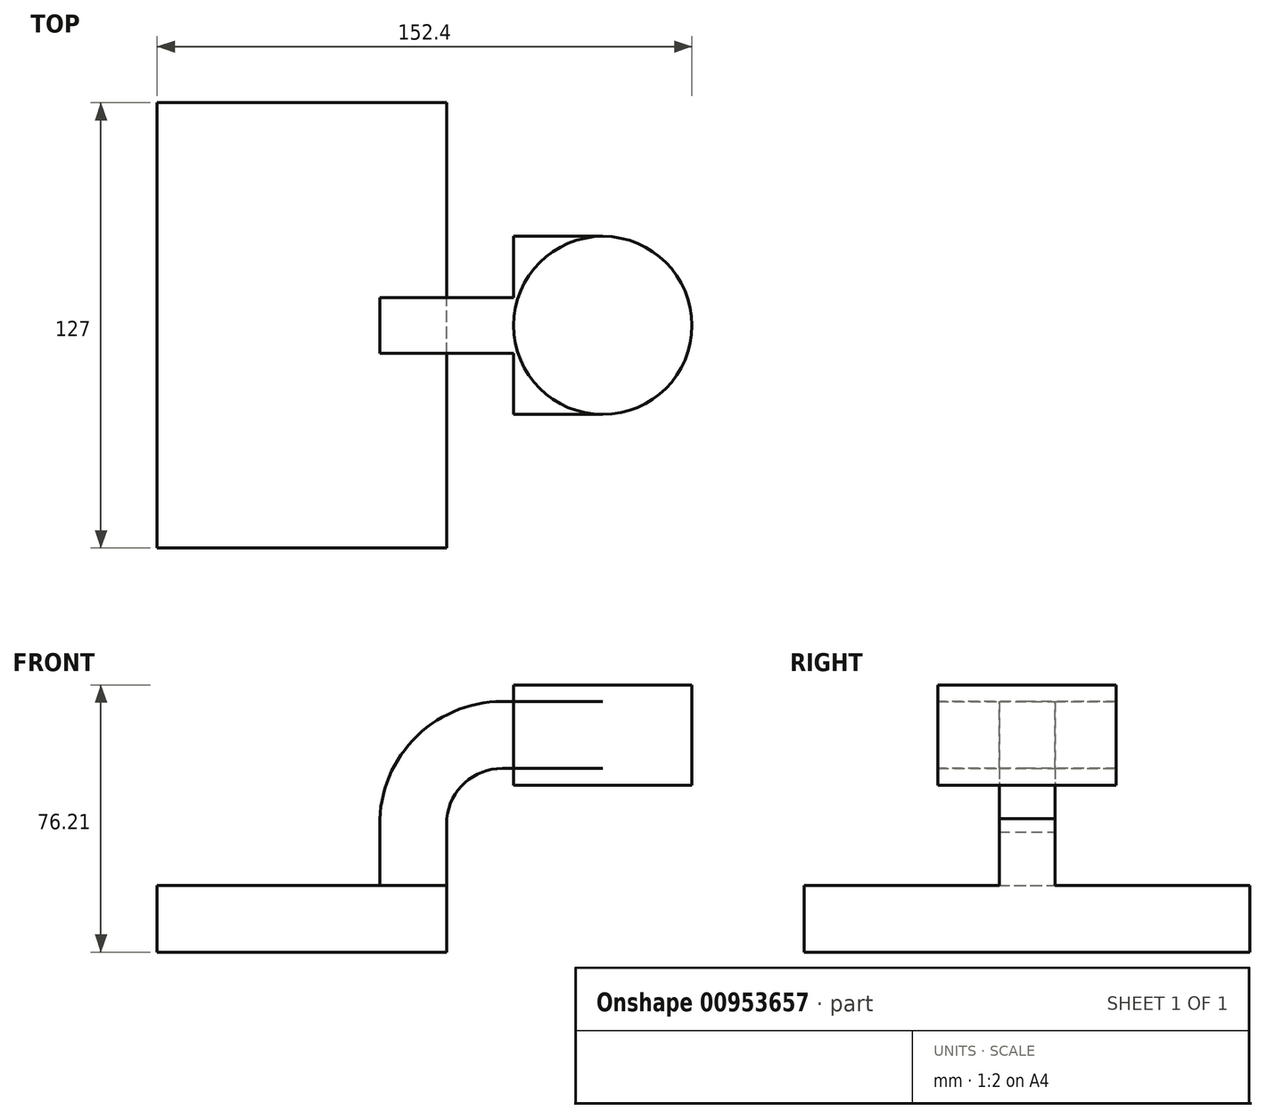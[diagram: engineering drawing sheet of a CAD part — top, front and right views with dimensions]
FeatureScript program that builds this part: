
annotation { "Feature Type Name" : "Feature", "Feature Type Description" : "" }
export const myFeature = defineFeature(function(context is Context, id is Id, definition is map)
    precondition{}
    {
        {
            var Q0;
            Q0=qCreatedBy(makeId("Front.planeOp"),FACE);
            var sketch = newSketch(context, id + "F0", { "sketchPlane" : qUnion([Q0])});
            skLineSegment(sketch, "E0.bottom", {"start": v(-41.28, -9.53) * mm, "end": v(41.28, -9.53) * mm});
            skLineSegment(sketch, "E0.top", {"start": v(-41.28, 9.53) * mm, "end": v(41.28, 9.53) * mm});
            skLineSegment(sketch, "E0.left", {"start": v(-41.28, -9.53) * mm, "end": v(-41.28, 9.53) * mm});
            skLineSegment(sketch, "E0.right", {"start": v(41.28, -9.53) * mm, "end": v(41.28, 9.53) * mm});
            skPoint(sketch, "E0.middle", {"position": v(0, 0) * mm});
            skLineSegment(sketch, "E1.bottom", {"start": v(60.33, 38.1) * mm, "end": v(111.12, 38.1) * mm});
            skLineSegment(sketch, "E1.top", {"start": v(60.33, 66.67) * mm, "end": v(111.12, 66.67) * mm});
            skLineSegment(sketch, "E1.left", {"start": v(60.33, 38.1) * mm, "end": v(60.33, 66.67) * mm});
            skLineSegment(sketch, "E1.right", {"start": v(111.12, 38.1) * mm, "end": v(111.12, 66.67) * mm});
            skPoint(sketch, "E1.middle", {"position": v(85.72, 52.39) * mm});
            skPoint(sketch, "E2.middle", {"position": v(41.28, 9.53) * mm});
            skArc(sketch, "E3", {"start": v(41.27, 28.54) * mm, "mid": v(46.4, 38.76) * mm, "end": v(57.08, 42.88) * mm});
            skLineSegment(sketch, "E4", {"start": v(57.08, 42.88) * mm, "end": v(85.72, 42.88) * mm});
            skLineSegment(sketch, "E5", {"start": v(41.28, 9.53) * mm, "end": v(41.27, 28.54) * mm});
            skArc(sketch, "E6.0", {"start": v(22.22, 24.72) * mm, "mid": v(31.59, 50.88) * mm, "end": v(57.08, 61.93) * mm});
            skLineSegment(sketch, "E6.1", {"start": v(22.23, 9.52) * mm, "end": v(22.22, 24.72) * mm});
            skLineSegment(sketch, "E7.0", {"start": v(57.08, 61.93) * mm, "end": v(85.72, 61.93) * mm});
            skLineSegment(sketch, "E8", {"start": v(85.72, 38.1) * mm, "end": v(85.72, 66.67) * mm});
            skFitSpline(sketch, "E9", {"points": [v(57.08, 61.93) * mm, v(-41.28, 9.53) * mm], "startDerivative": vector(-128.94, 14.74) * mm, "endDerivative": vector(-5.3, -85.67) * mm});
            skSolve(sketch);
        }
        {
            var Q0;
            Q0=makeQuery(id+"F0.imprint","IMPRINT",FACE,{"disambiguationData":[TD([[makeQuery(id+"F0.imprint","IMPRINT",EDGE,{"derivedFrom":sQuery(id+"F0.wireOp",EDGE,"E0.bottom")}),1.0]])]});
            extrude(context, id + "F1", {"entities" : qUnion([Q0]), "endBound" : BoundingType.SYMMETRIC, "depth" : 127 * mm, "offsetDistance" : 25.4 * mm});
        }
        {
            var Q0;
            {var subQ1=sQuery(id+"F0.wireOp",EDGE,"E3");Q0=makeQuery(id+"F0.imprint","IMPRINT",FACE,{"disambiguationData":[TD([[makeQuery(id+"F0.imprint","IMPRINT",EDGE,{"derivedFrom":subQ1}),1.0]])]});}
            var Q1;
            {var subQ0=sQuery(id+"F0.wireOp",EDGE,"E4");var subQ1=sQuery(id+"F0.wireOp",EDGE,"E1.left");var subQ2=makeQuery(id+"F0.imprint","INTERSECT",VERTEX,{"derivedFrom":[subQ1,subQ0]});Q1=makeQuery(id+"F0.imprint","IMPRINT",FACE,{"disambiguationData":[TD([[makeQuery(id+"F0.imprint","IMPRINT",EDGE,{"disambiguationData":[TD([[subQ2,-1.0]])],"derivedFrom":subQ1}),-1.0]])]});}
            extrude(context, id + "F2", {"entities" : qUnion([Q0, Q1]), "operationType" : NewBodyOperationType.ADD, "endBound" : BoundingType.SYMMETRIC, "depth" : 50.8 * mm, "offsetDistance" : 25.4 * mm});
        }
        {
            var Q0;
            Q0=makeQuery(id+"F0.imprint","IMPRINT",FACE,{"disambiguationData":[TD([[makeQuery(id+"F0.imprint","IMPRINT",EDGE,{"derivedFrom":sQuery(id+"F0.wireOp",EDGE,"E6.0")}),1.0]])]});
            extrude(context, id + "F3", {"entities" : qUnion([Q0]), "operationType" : NewBodyOperationType.ADD, "endBound" : BoundingType.SYMMETRIC, "depth" : 15.88 * mm, "offsetDistance" : 25.4 * mm});
        }
        {
            var Q0;
            {var subQ0=sQuery(id+"F0.wireOp",EDGE,"E1.right");Q0=makeQuery(id+"F0.imprint","IMPRINT",FACE,{"disambiguationData":[TD([[makeQuery(id+"F0.imprint","IMPRINT",EDGE,{"derivedFrom":subQ0}),1.0]])]});}
            var Q1;
            Q1=sQuery(id+"F0.wireOp",EDGE,"E8");
            revolve(context, id + "F4", {"operationType" : NewBodyOperationType.ADD, "surfaceOperationType" : NewSurfaceOperationType.NEW, "entities" : qUnion([Q0]), "axis" : qUnion([Q1]), "revolveType" : RevolveType.FULL});
        }
    });
